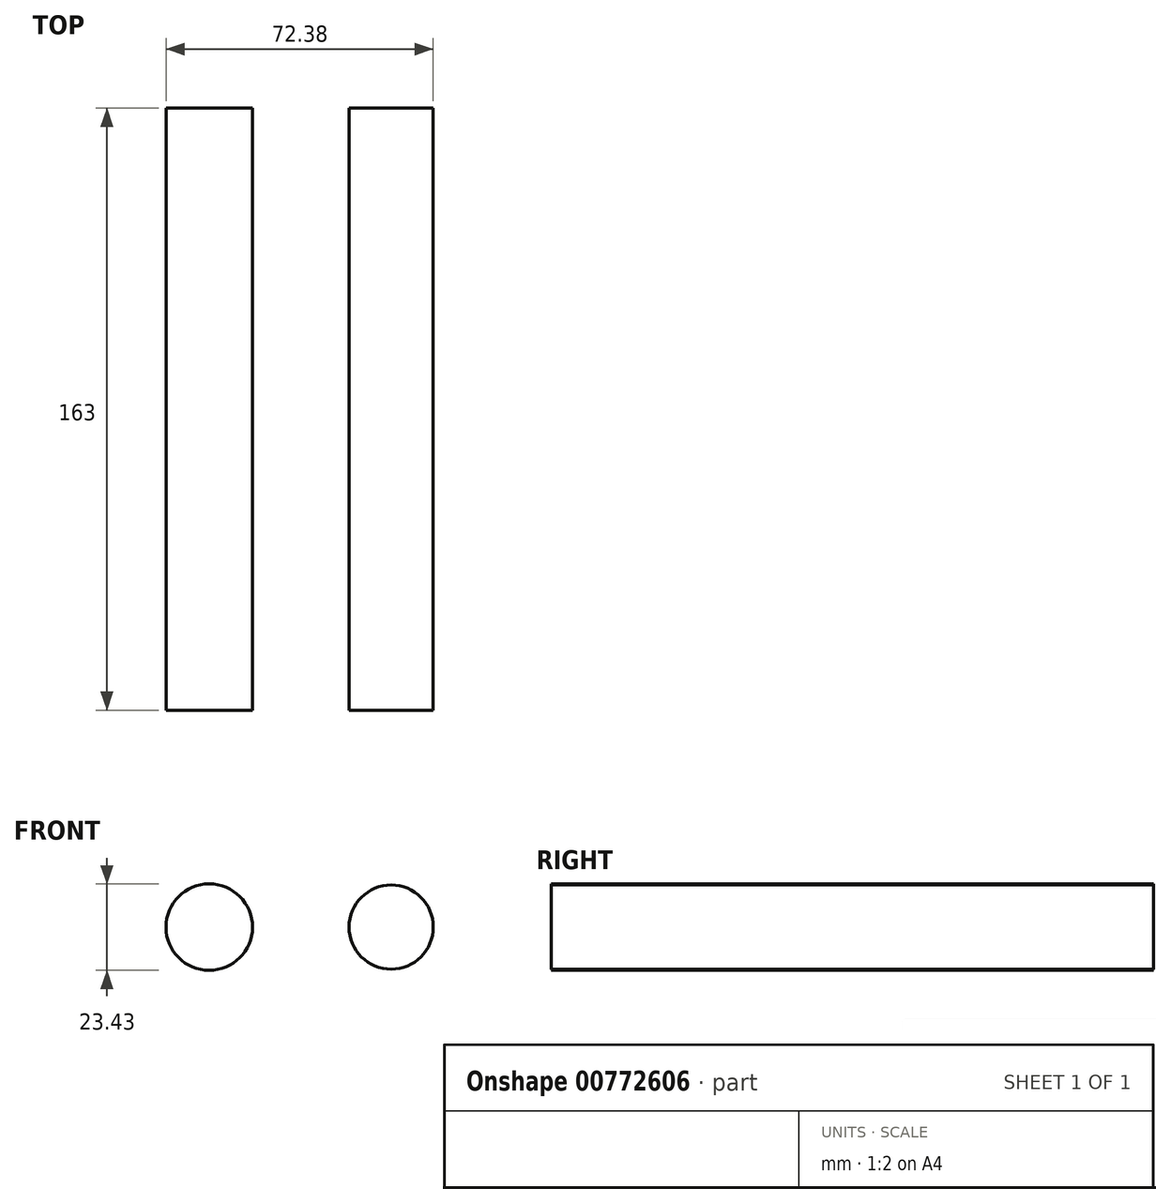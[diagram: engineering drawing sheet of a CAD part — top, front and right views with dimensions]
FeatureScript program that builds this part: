
annotation { "Feature Type Name" : "Feature", "Feature Type Description" : "" }
export const myFeature = defineFeature(function(context is Context, id is Id, definition is map)
    precondition{}
    {
        {
            var Q0;
            Q0=qCreatedBy(makeId("Front.planeOp"),FACE);
            var sketch = newSketch(context, id + "F0", { "sketchPlane" : qUnion([Q0])});
            skCircle(sketch, "E0", {"center": v(0, 0) * mm, "radius": 68.1 * mm});
            skCircle(sketch, "E1", {"center": v(-27.19, 12) * mm, "radius": 11.71 * mm});
            skCircle(sketch, "E2", {"center": v(22.08, 12) * mm, "radius": 11.4 * mm});
            skSolve(sketch);
        }
        {
            var Q0;
            Q0=makeQuery(id+"F0.imprint","IMPRINT",FACE,{"disambiguationData":[TD([[makeQuery(id+"F0.imprint","IMPRINT",EDGE,{"derivedFrom":sQuery(id+"F0.wireOp",EDGE,"E1")}),1.0]])]});
            var Q1;
            Q1=makeQuery(id+"F0.imprint","IMPRINT",FACE,{"disambiguationData":[TD([[makeQuery(id+"F0.imprint","IMPRINT",EDGE,{"derivedFrom":sQuery(id+"F0.wireOp",EDGE,"E2")}),1.0]])]});
            extrude(context, id + "F1", {"entities" : qUnion([Q0, Q1]), "depth" : 163 * mm, "offsetDistance" : 25 * mm});
        }
    });
